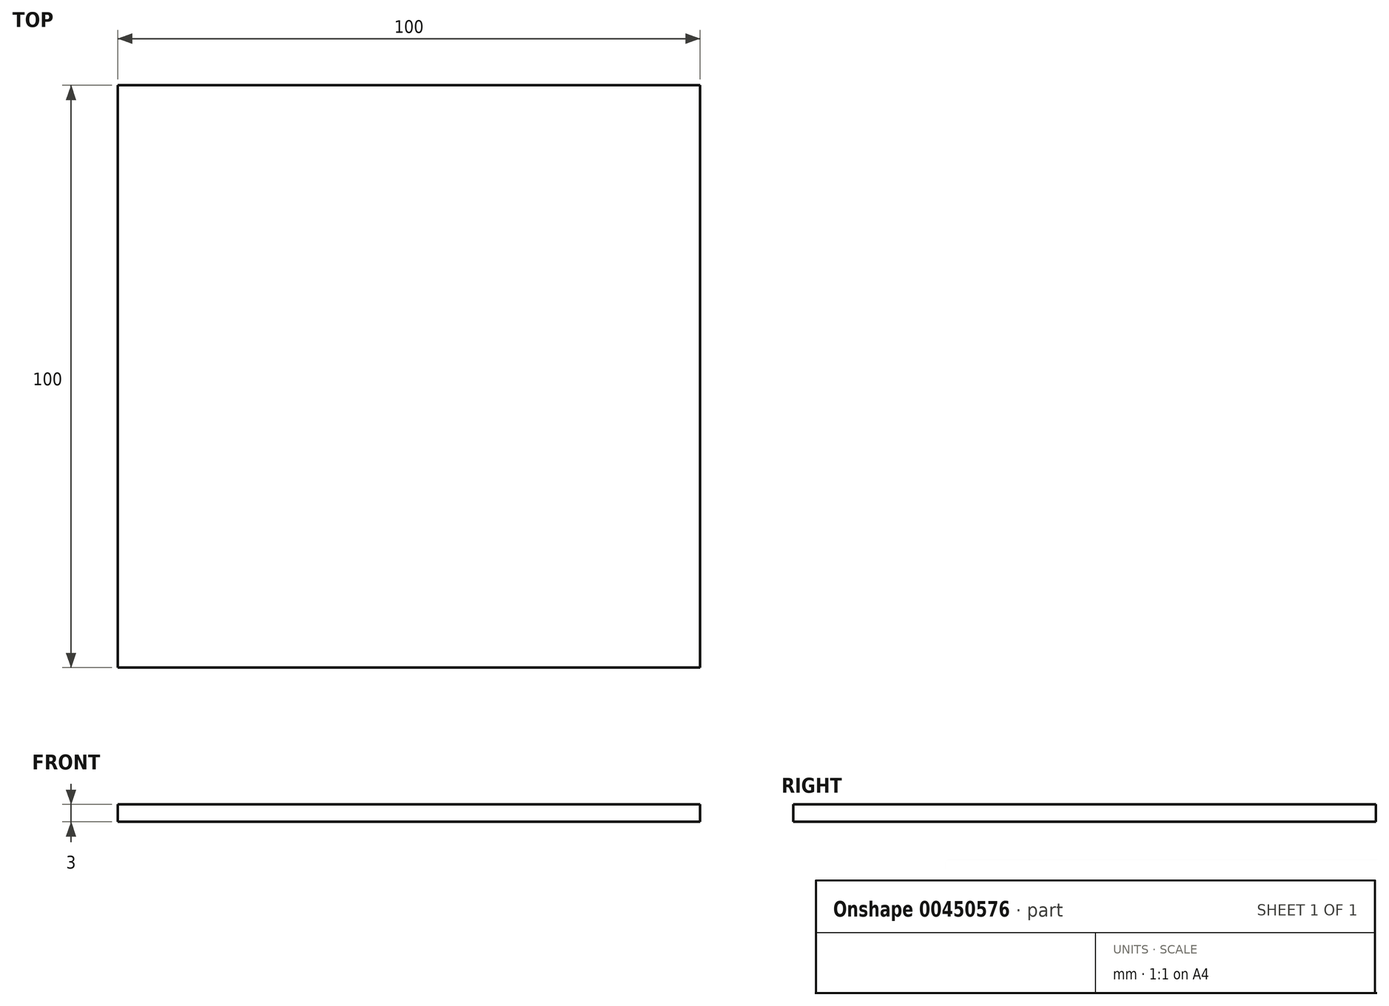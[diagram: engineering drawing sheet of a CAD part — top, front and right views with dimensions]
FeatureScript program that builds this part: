
annotation { "Feature Type Name" : "Feature", "Feature Type Description" : "" }
export const myFeature = defineFeature(function(context is Context, id is Id, definition is map)
    precondition{}
    {
        {
            var Q0;
            Q0=qCreatedBy(makeId("Top.planeOp"),FACE);
            var sketch = newSketch(context, id + "F0", { "sketchPlane" : qUnion([Q0])});
            skLineSegment(sketch, "E0.bottom", {"start": v(-50, 50) * mm, "end": v(50, 50) * mm});
            skLineSegment(sketch, "E0.top", {"start": v(-50, -50) * mm, "end": v(50, -50) * mm});
            skLineSegment(sketch, "E0.left", {"start": v(-50, 50) * mm, "end": v(-50, -50) * mm});
            skLineSegment(sketch, "E0.right", {"start": v(50, 50) * mm, "end": v(50, -50) * mm});
            skSolve(sketch);
        }
        {
            var Q0;
            Q0=makeQuery(id+"F0.imprint","IMPRINT",FACE,{"disambiguationData":[TD([[makeQuery(id+"F0.imprint","IMPRINT",EDGE,{"derivedFrom":sQuery(id+"F0.wireOp",EDGE,"E0.bottom")}),-1.0]])]});
            extrude(context, id + "F1", {"entities" : qUnion([Q0]), "depth" : 3 * mm});
        }
    });
